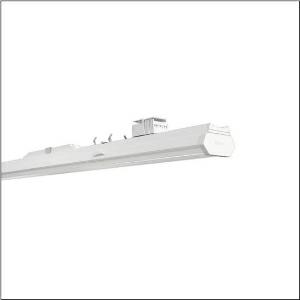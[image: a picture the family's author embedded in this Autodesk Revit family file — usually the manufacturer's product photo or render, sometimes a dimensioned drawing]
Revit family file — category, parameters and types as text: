
# Revit family: licross_r__11_protected_mo_51td1bdn68xg_8e9f
name_source: partatom
category: Lighting Fixtures
units: mm (PartAtom-declared; Revit-internal decimal feet)

## family parameters
Cut with Voids When Loaded = No
Host = Face
Light Source = No
Part Type = Normal
Room Calculation Point = No
Round Connector Dimension = Use Diameter
Shared = No

## types (1)
- --- (1 x LED, 8310 lm, 51.3 W, 6500K)
    Apparent Load = 51 VA
    CIE Flux Codes = 54 82 95 97 100
    Color Rendering = 80
    Color Temperature = 6500K
    Default Elevation = 1800 mm
    Description = Licross® 11 Protected MO, luminaire insert, of sheet steel, galvanised, coil coated, white, length: 1.500mm, width: 90mm, height: 101mm, LED rated luminous flux: 8.310lm, light colour: 865, control gear: DALI 2, with plug, 5-pole, with phase selection, mains connection: 220..240V, AC, 50/60Hz, rated input power: 51W, internal wiring halogen-free, primary optical cover: cover, of PMMA, light emission: direct distribution, primary light characteristic: symmetric, protection rating (complete): IP54, insulation class (complete): insulation class I (protective earthing), certification: CE, ENEC, VDE, UKCA, protection symbol: D if used in an environment with non-conductive dust loads with corresponding accessories, impact resistance: IK06, permissible ambient temperature for indoor applications: -25..+35°C, corresponds to IFS (International Featured Standards) requirements for safety and quality in the food industry, reducing of maximum allowable ambient temperature of 5°C with ceiling mounting, LABS conformity tested according to VDMA 24364:2018-05, packaging unit: 1 piece
    Height = 92 mm
    Lamp = 1 x LED
    Lamp Light Flux = 8310 lm
    Lamp Power = 51.3 W
    Lamp count = 1
    Length = 1500 mm
    Luminous efficacy = 162 lm/W
    Manufacturer = Siteco
    ModVariant = No
    Model = 51TD1BDN68XG
    Mounting Place = Ceiling
    Mounting Type = Pendant
    Number of Poles = 1
    OnlyDefault = Yes
    Power Factor = 1
    Product Name = Licross® 11 Protected MO
    Product group = luminaire insert | ceiling pendant
    ProductGroupID = 902
    Protection Class = Protection class I
    Protection Degree = IP 54
    RLX_Detail_Level = 1
    RLX_Emergency_Light_Flux = 0 lm
    RLX_Emergency_Type = 0
    RLX_Emergency_Type_DB = No
    RlxData = <blob elided: 24505 chars, md5=ced6f84f>
    Socket = socket
    Standby Power = 0 W
    System Light Flux = 8310 lm
    System Power = 51 W
    Type Comments = factory setting: luminous flux: 100 % | dim-lin: 254 | 341 mA
    Type Image = l_1256145.jpg
    URL = http://relux.com
    VarID = @adj_069811
    Voltage = 0 V
    Weight = 0.00 kg
    Width = 88 mm

## geometry (parser evidence)
native form markers: Blend x4, Sweep x10
no freeform markers — native parametric forms only
